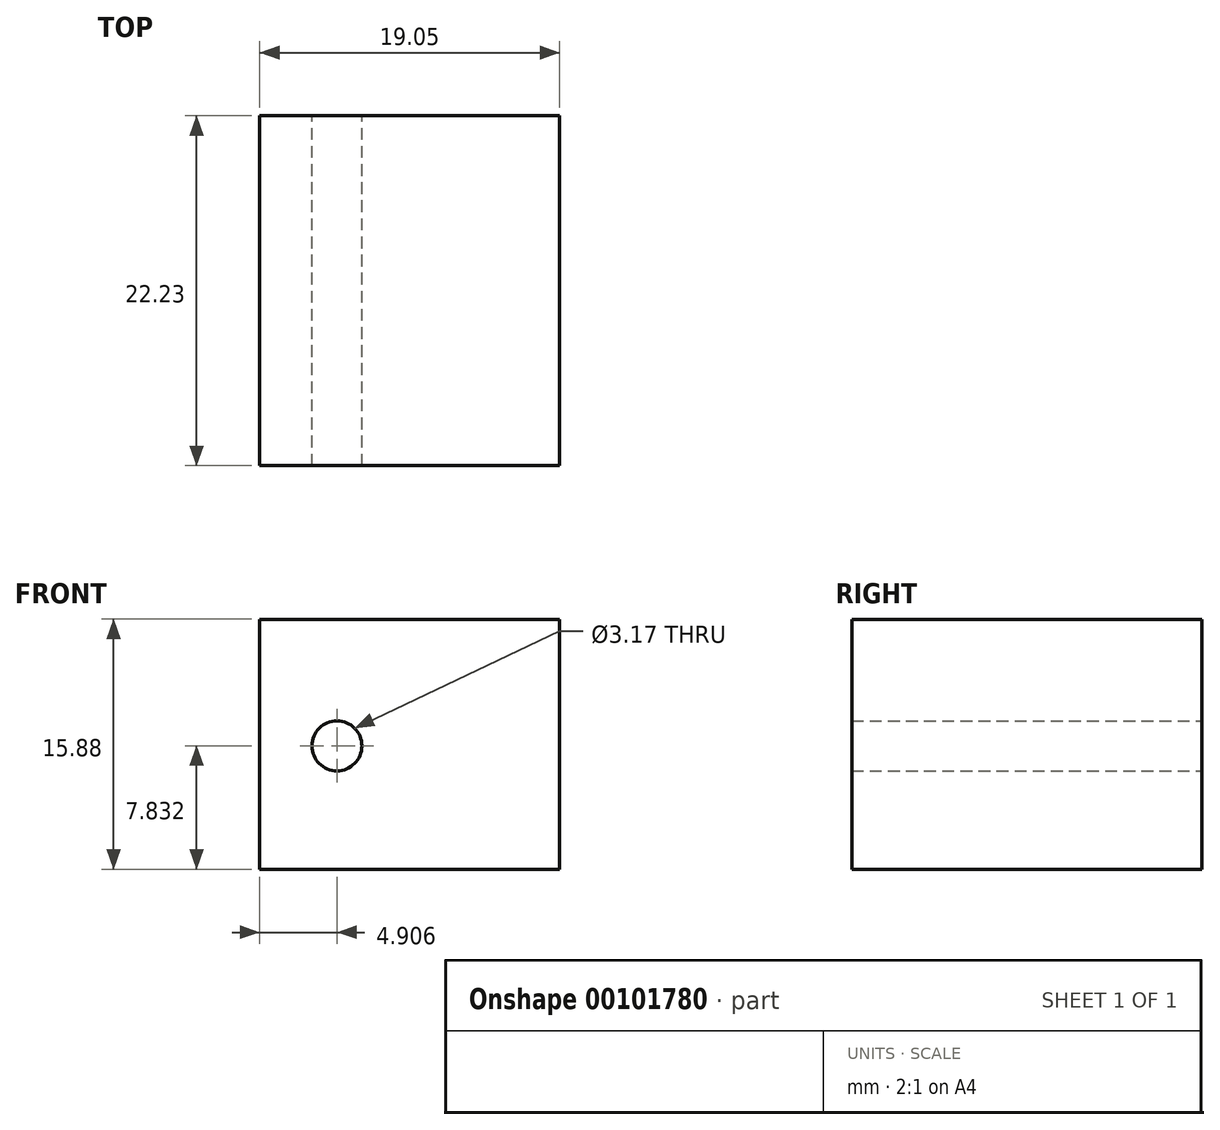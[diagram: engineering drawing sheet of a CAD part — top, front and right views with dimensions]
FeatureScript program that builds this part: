
annotation { "Feature Type Name" : "Feature", "Feature Type Description" : "" }
export const myFeature = defineFeature(function(context is Context, id is Id, definition is map)
    precondition{}
    {
        {
            var Q0;
            Q0=qCreatedBy(makeId("Front.planeOp"),FACE);
            var sketch = newSketch(context, id + "F0", { "sketchPlane" : qUnion([Q0])});
            skLineSegment(sketch, "E0.bottom", {"start": v(-41.78, 15.88) * mm, "end": v(-22.73, 15.88) * mm});
            skLineSegment(sketch, "E0.top", {"start": v(-41.78, 0) * mm, "end": v(-22.73, 0) * mm});
            skLineSegment(sketch, "E0.left", {"start": v(-41.78, 15.88) * mm, "end": v(-41.78, 0) * mm});
            skLineSegment(sketch, "E0.right", {"start": v(-22.73, 15.88) * mm, "end": v(-22.73, 0) * mm});
            skCircle(sketch, "E1", {"center": v(-36.87, 7.83) * mm, "radius": 1.59 * mm});
            skSolve(sketch);
        }
        {
            var Q0;
            Q0=makeQuery(id+"F0.imprint","IMPRINT",FACE,{"disambiguationData":[TD([[makeQuery(id+"F0.imprint","IMPRINT",EDGE,{"derivedFrom":sQuery(id+"F0.wireOp",EDGE,"E0.bottom")}),-1.0]])]});
            extrude(context, id + "F1", {"entities" : qUnion([Q0]), "depth" : 22.22 * mm});
        }
    });
